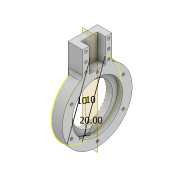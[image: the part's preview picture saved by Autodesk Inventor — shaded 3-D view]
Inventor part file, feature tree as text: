
AUTODESK INVENTOR PART (.ipt)
format: ipt  version: 2022 (Build 260153000, 153)  size: 220,160 bytes
history: native  units: mm
features: extrude x7, sketch x7, fillet x2, pattern_circular x1, plane x1, mirror x1, projected_geometry x1
ambient origin geometry x8: Origin, YZ Plane, XZ Plane, XY Plane, X Axis, Y Axis, Z Axis, Center Point
bodies: Solid1 (feature_tree)
feature tree (20):
  extrude  "Extrusion1"  Depth=12.0mm
  extrude  "Extrusion2"  Depth=8.0mm TaperAngle=0.0deg
  extrude  "Extrusion3"  Depth=6.0mm TaperAngle=0.0deg
  pattern_circular  "Circular Pattern1"  Count=10  [1 undecoded]
  plane  "Work Plane1"
  sketch  "Sketch4"  dims[d8=3.2mm]
  extrude  "Extrusion4"  Depth=40.0mm
  extrude  "Extrusion5"  Depth=10.0mm
  fillet  "Fillet1"  Radius=10.1mm
  extrude  "Extrusion6"  Depth=8.0mm
  fillet  "Fillet2"  Radius=8.0mm
  extrude  "Extrusion7"  Depth=10.0mm TaperAngle=0.0deg
  mirror  "Mirror1"
  sketch  "Sketch8"  dims[d16=10.1mm d17=20.2mm d18=10.1mm d20=8.0mm d21=8.0mm d22=100.0mm d23=0.0mm d24=30.0mm d25=0.0mm d26=5.0mm d27=3.2mm d28=3.2mm d29=3.2mm d30=4.0mm d31=4.0mm d32=15.0mm d33=4.0mm d34=9.0mm d35=4.0mm d36=0.0mm d37=5.0mm d38=100.0mm d39=0.0mm d40=3.490659mm d41=10.0mm d42=10.0mm]
  sketch  "Sketch1"  dims[d0=62.5mm d1=12.0mm]
  sketch  "Sketch2"  dims[d2=50.0mm d3=8.0mm d4=0.0mm]
  projected_geometry  "Projected Loop1"
  sketch  "Sketch3"  dims[d5=62.5mm d6=6.0mm d7=0.0mm]
  sketch  "Sketch6"  dims[d9=37.0mm d10=100.0mm d11=0.0mm]
  sketch  "Sketch7"  dims[d12=60.0mm d13=360.0deg d15=40.0mm]
note: 1 required parameter value undecoded (feature->parameter linkage not recoverable at this tier; creation-order binding heuristic only, values carry confidence <= 0.55)
